# Revit family: 202_KW-_
name_source: partatom
category: Air Terminals
units: mm (PartAtom-declared; Revit-internal decimal feet)

## family parameters
Always vertical = Yes
Cut with Voids When Loaded = No
Part Type = Normal
Room Calculation Point = Yes
Round Connector Dimension = Use Diameter
Shared = No
Work Plane-Based = No

## types (7) — shared parameters
C = 12 mm  [stored 0.0393701 ft]
CAT0 = Yes
CL_Location_5000 = 5000 mm  [stored 16.4042 ft]
DP = 5 mm  [stored 0.0164042 ft]
Description = AIR EXHAUST VALVE
GAP = 2 mm  [stored 0.00656168 ft]
GAP__ve = -2 mm  [stored -0.00656168 ft]
L_ARR = 400 mm  [stored 1.31234 ft]
Manufacturer = Alnor
QmdConnectorList = 201;D
URL = http://www.ventilation-alnor.co.uk
W_ARR = 400 mm  [stored 1.31234 ft]
XRefLineVPlnId = 7453
YRefLineVPlnId = 7456
ZD1 = 6 mm  [stored 0.019685 ft]
ZD2 = 9 mm  [stored 0.0295276 ft]
magiPartTypeId = 202
magiProductFamilyId = KW-*
zero-valued in all types: CLBTZ, H_ARR

## per-type parameters (varying)
| type | B | D | D1 | R1 | R12 | RB |
| KW-080 | 115 mm  [stored 0.377297 ft] | 80 mm | 70 mm  [stored 0.229659 ft] | 40 mm  [stored 0.131234 ft] | 16 mm  [stored 0.0524934 ft] | 50 mm |
| KW-250 | 302 mm | 250 mm | 240 mm | 125 mm  [stored 0.410105 ft] | 50 mm | 140 mm |
| KW-200 | 248 mm | 200 mm | 190 mm | 100 mm  [stored 0.328084 ft] | 40 mm  [stored 0.131234 ft] | 114 mm |
| KW-160 | 212 mm | 160 mm | 150 mm | 80 mm  [stored 0.262467 ft] | 32 mm | 95 mm |
| KW-150 | 202 mm | 150 mm | 140 mm | 75 mm | 30 mm  [stored 0.0984252 ft] | 90 mm |
| KW-125 | 164 mm | 125 mm | 115 mm  [stored 0.377297 ft] | 63 mm | 25 mm  [stored 0.082021 ft] | 74 mm |
| KW-100 | 137 mm | 100 mm | 90 mm | 50 mm | 20 mm  [stored 0.0656168 ft] | 61 mm |

note: column(s) folded — value = type name in every type: MC Product Code, magiProductId

note: [stored X ft] marks values corroborated as IEEE doubles in the binary element streams (Revit-internal decimal feet)

## geometry (parser evidence)
native form markers: Blend x4, Sweep x2
no freeform markers — native parametric forms only
